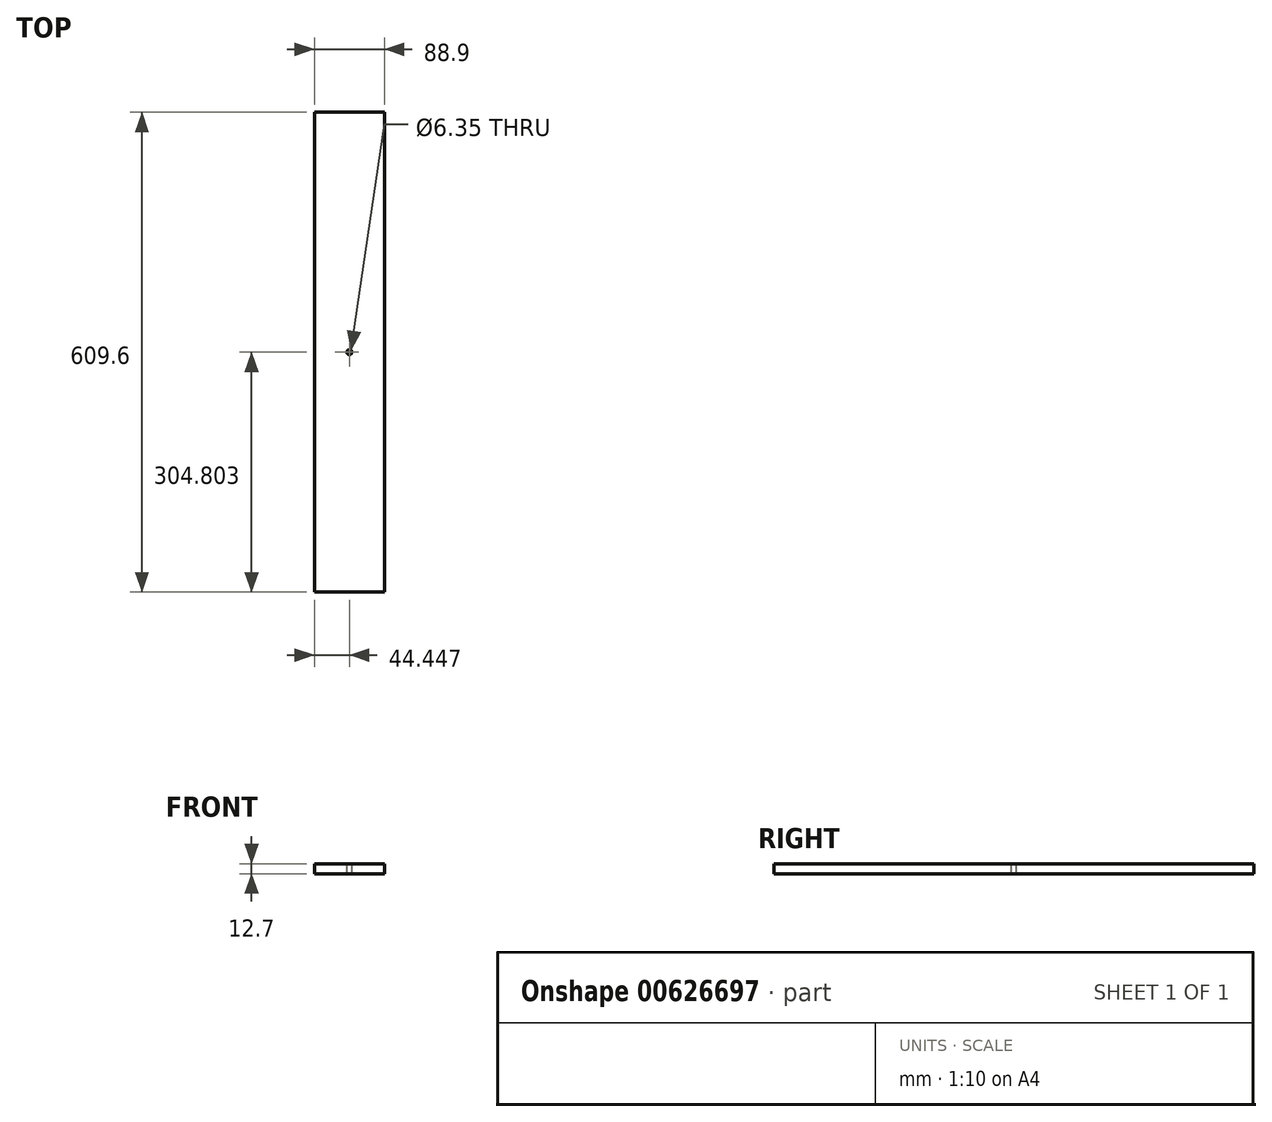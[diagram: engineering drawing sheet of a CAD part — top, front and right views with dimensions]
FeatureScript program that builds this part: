
annotation { "Feature Type Name" : "Feature", "Feature Type Description" : "" }
export const myFeature = defineFeature(function(context is Context, id is Id, definition is map)
    precondition{}
    {
        {
            var Q0;
            Q0=qCreatedBy(makeId("Top.planeOp"),FACE);
            var sketch = newSketch(context, id + "F0", { "sketchPlane" : qUnion([Q0])});
            skLineSegment(sketch, "E0.bottom", {"start": v(-79.2, -195.28) * mm, "end": v(9.7, -195.28) * mm});
            skLineSegment(sketch, "E0.top", {"start": v(-79.2, 414.32) * mm, "end": v(9.7, 414.32) * mm});
            skLineSegment(sketch, "E0.left", {"start": v(-79.2, -195.28) * mm, "end": v(-79.2, 414.32) * mm});
            skLineSegment(sketch, "E0.right", {"start": v(9.7, -195.28) * mm, "end": v(9.7, 414.32) * mm});
            skSolve(sketch);
        }
        {
            var Q0;
            Q0=makeQuery(id+"F0.imprint","IMPRINT",FACE,{"disambiguationData":[TD([[makeQuery(id+"F0.imprint","IMPRINT",EDGE,{"derivedFrom":sQuery(id+"F0.wireOp",EDGE,"E0.bottom")}),1.0]])]});
            extrude(context, id + "F1", {"entities" : qUnion([Q0]), "depth" : 12.7 * mm, "offsetDistance" : 25.4 * mm});
        }
        {
            var Q0;
            Q0=makeQuery(id+"F1.opExtrude","CAP_FACE",FACE,{"disambiguationData":[OSD([sQuery(id+"F0.wireOp",EDGE,"E0.bottom"),sQuery(id+"F0.wireOp",EDGE,"E0.top"),sQuery(id+"F0.wireOp",EDGE,"E0.left"),sQuery(id+"F0.wireOp",EDGE,"E0.right")])],"isStart":false});
            var sketch = newSketch(context, id + "F2", { "sketchPlane" : qUnion([Q0])});
            skLineSegment(sketch, "E1", {"start": v(-34.75, -195.28) * mm, "end": v(-34.75, 414.32) * mm});
            skLineSegment(sketch, "E2", {"start": v(-79.2, 109.52) * mm, "end": v(9.7, 109.52) * mm});
            skCircle(sketch, "E3", {"center": v(-34.75, 109.52) * mm, "radius": 3.18 * mm});
            skSolve(sketch);
        }
        {
            var Q0;
            Q0 = qSketchRegion(id + "F2", true);
            extrude(context, id + "F3", {"entities" : qUnion([Q0]), "operationType" : NewBodyOperationType.REMOVE, "oppositeDirection" : true, "depth" : 25.4 * mm, "offsetDistance" : 25.4 * mm});
        }
    });
